# Revit family: Furniture-Lighted_Medicine_Cabinet-KOHLER-Grooming-K-33690K_1
name_source: partatom
category: Lighting Fixtures
units: mm (PartAtom-declared; Revit-internal decimal feet)

## family parameters
Cut with Voids When Loaded = No
Host = Face
Light Source = Yes
OmniClass Number = 23.25.53.11.13.11
OmniClass Title = Medicine Cabinet
Part Type = Normal
Room Calculation Point = No
Round Connector Dimension = Use Diameter
Shared = No

## types (2) — shared parameters
ADA Compliant = No
Apparent Load = 55 VA
Assembly Code = E2010
Color Filter = 16777215
Date Modified = 06/05/2023
Default Elevation = 60"
Depth = 6 1/8"
Dimming Lamp Color Temperature Shift = Incandescent Lamp Curve
Electrical Connector = Yes
Electrical Note = One Dedicated Circuit Required
Emit from Line Length = 24"
Finish = Kohler-Metal-NA-Black
Hardware Included = No
Height = 31 1/2"
Lamp = LED
Light Source Symbol Size = 3 15/16"
Manufacturer = Kohler Co.
Master Format 2014 = 41 53 13
Master Format 2014 Name = Storage Cabinets
Material = Aluminium
Product Name = Grooming
URL = https://www.kohlerasiapacific.com
Voltage = 240 V
WaterSense Certified = No
Wattage Comments = 55W
Width = 23 3/8"

## per-type parameters (varying)
| type | Description | Model | Type |
| Left Side, NA-Black | 600mm Lighted Cabinet Left Open | K-33690K-L-NA | 1 |
| Right Side, NA-Black | 600mm Lighted Cabinet Right Open | K-33690K-R-NA | 2 |

## geometry (parser evidence)
native form markers: Sweep x7
no freeform markers — native parametric forms only
